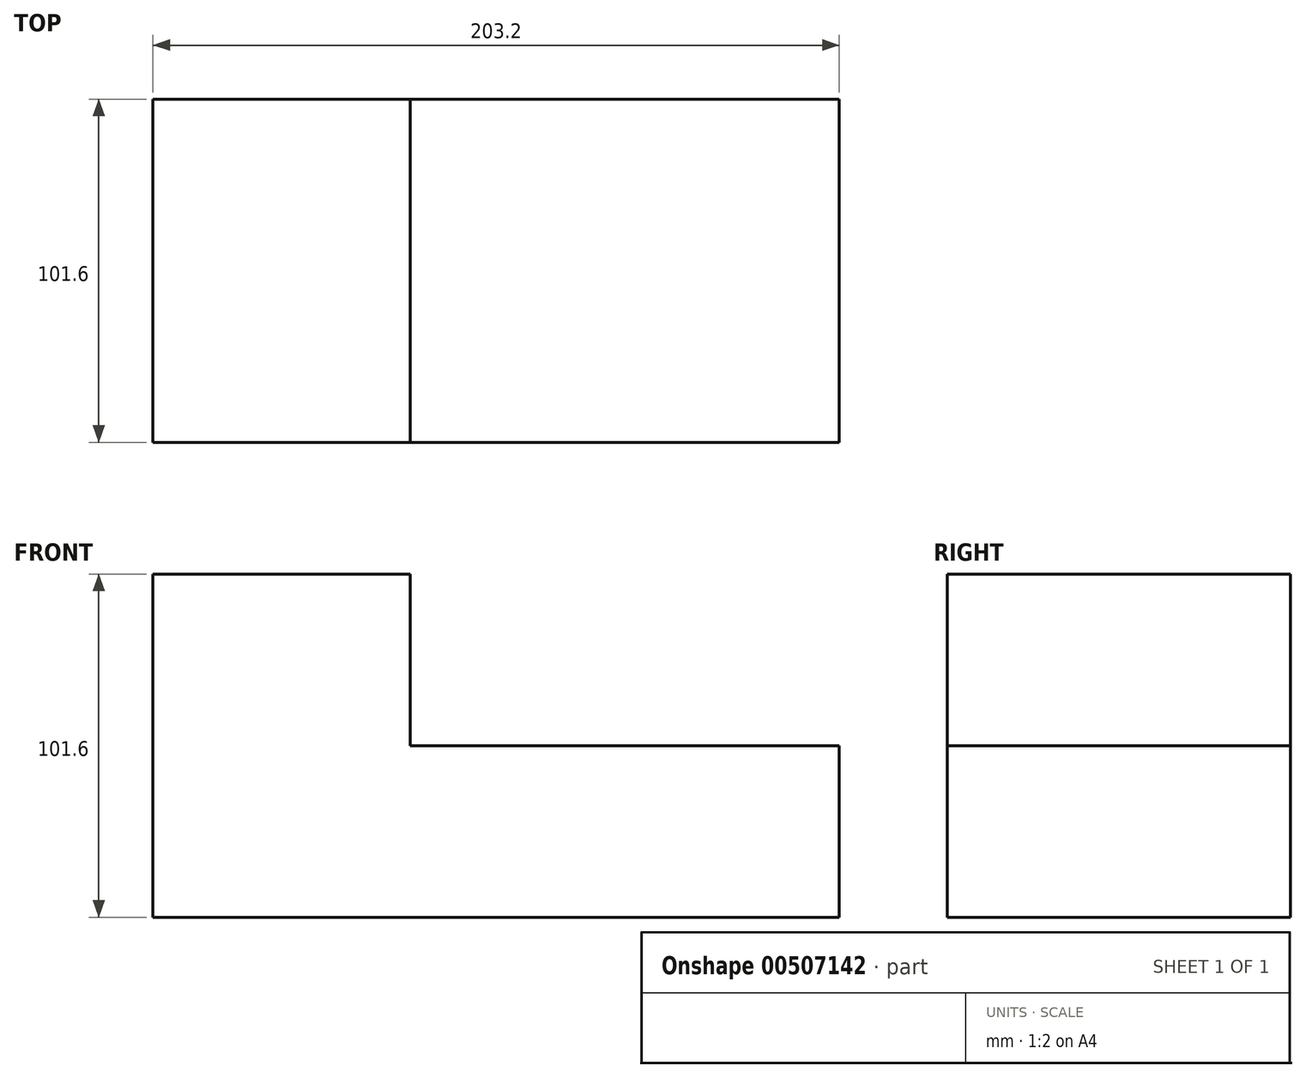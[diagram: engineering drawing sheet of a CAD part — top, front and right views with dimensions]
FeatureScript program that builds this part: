
annotation { "Feature Type Name" : "Feature", "Feature Type Description" : "" }
export const myFeature = defineFeature(function(context is Context, id is Id, definition is map)
    precondition{}
    {
        {
            var Q0;
            Q0=qCreatedBy(makeId("Front.planeOp"),FACE);
            var sketch = newSketch(context, id + "F0", { "sketchPlane" : qUnion([Q0])});
            skLineSegment(sketch, "E0.bottom", {"start": v(0, 0) * mm, "end": v(-127, 0) * mm});
            skLineSegment(sketch, "E0.top", {"start": v(0, 50.8) * mm, "end": v(-127, 50.8) * mm});
            skLineSegment(sketch, "E0.left", {"start": v(0, 0) * mm, "end": v(0, 50.8) * mm});
            skLineSegment(sketch, "E0.right", {"start": v(-127, 0) * mm, "end": v(-127, 50.8) * mm});
            skLineSegment(sketch, "E1.bottom", {"start": v(-127, 0) * mm, "end": v(-203.2, 0) * mm});
            skLineSegment(sketch, "E1.top", {"start": v(-127, 101.6) * mm, "end": v(-203.2, 101.6) * mm});
            skLineSegment(sketch, "E1.left", {"start": v(-127, 0) * mm, "end": v(-127, 101.6) * mm});
            skLineSegment(sketch, "E1.right", {"start": v(-203.2, 0) * mm, "end": v(-203.2, 101.6) * mm});
            skSolve(sketch);
        }
        {
            var Q0;
            Q0 = qSketchRegion(id + "F0", true);
            extrude(context, id + "F1", {"entities" : qUnion([Q0]), "depth" : 101.6 * mm});
        }
    });
